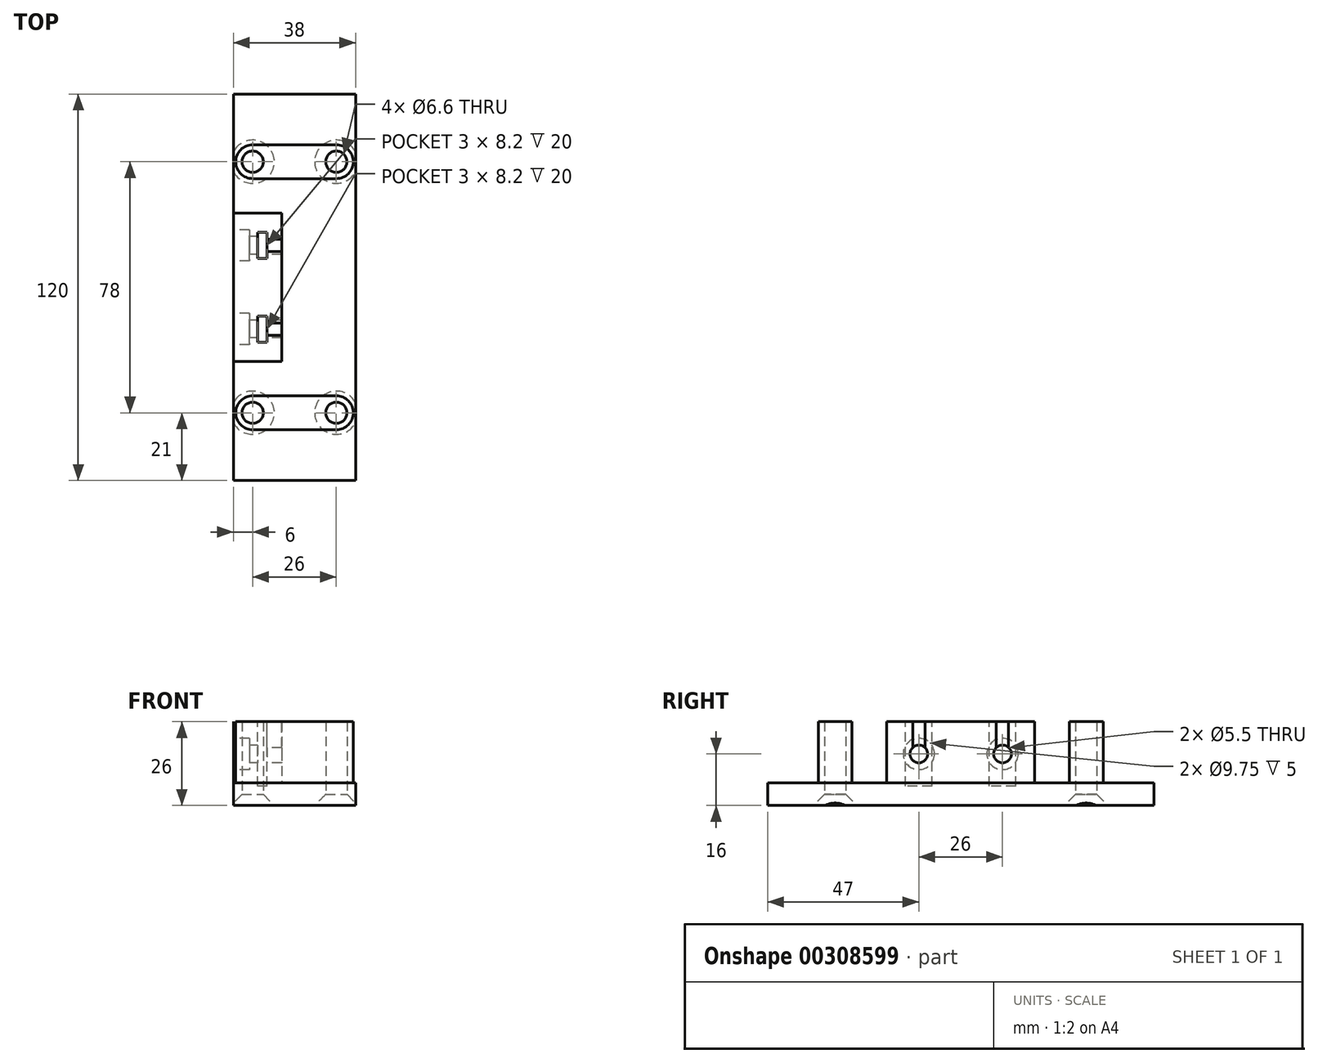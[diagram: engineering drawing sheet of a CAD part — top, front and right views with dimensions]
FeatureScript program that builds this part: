
annotation { "Feature Type Name" : "Feature", "Feature Type Description" : "" }
export const myFeature = defineFeature(function(context is Context, id is Id, definition is map)
    precondition{}
    {
        {
            var Q0;
            Q0=qCreatedBy(makeId("Top.planeOp"),FACE);
            var sketch = newSketch(context, id + "F0", { "sketchPlane" : qUnion([Q0])});
            skCircle(sketch, "E0", {"center": v(0, 0) * mm, "radius": 70.5 * mm});
            skCircle(sketch, "E1", {"center": v(0, 0) * mm, "radius": 60.75 * mm});
            skLineSegment(sketch, "E2", {"start": v(0, 0) * mm, "end": v(-222, 0) * mm, "construction": true});
            skPoint(sketch, "E3", {"position": v(-80, 0) * mm});
            skCircle(sketch, "E4", {"center": v(0, 0) * mm, "radius": 63.9 * mm});
            skPoint(sketch, "E5", {"position": v(-66.29, 24) * mm});
            skPoint(sketch, "E6", {"position": v(-55.8, 24) * mm});
            skPoint(sketch, "E7", {"position": v(-99, 0) * mm});
            skLineSegment(sketch, "E8.bottom", {"start": v(-118, 45.5) * mm, "end": v(-80, 45.5) * mm, "construction": true});
            skLineSegment(sketch, "E8.top", {"start": v(-118, -45.5) * mm, "end": v(-80, -45.5) * mm, "construction": true});
            skLineSegment(sketch, "E8.left", {"start": v(-118, 45.5) * mm, "end": v(-118, -45.5) * mm, "construction": true});
            skLineSegment(sketch, "E8.right", {"start": v(-80, 45.5) * mm, "end": v(-80, -45.5) * mm, "construction": true});
            skLineSegment(sketch, "E9.bottom", {"start": v(-86, 39) * mm, "end": v(-112, 39) * mm, "construction": true});
            skLineSegment(sketch, "E9.top", {"start": v(-86, -39) * mm, "end": v(-112, -39) * mm});
            skLineSegment(sketch, "E9.left", {"start": v(-86, 44) * mm, "end": v(-86, -44) * mm, "construction": true});
            skLineSegment(sketch, "E9.right", {"start": v(-112, 44) * mm, "end": v(-112, -44) * mm, "construction": true});
            skCircle(sketch, "E10", {"center": v(-112, 39) * mm, "radius": 2.5 * mm});
            skCircle(sketch, "E11", {"center": v(-86, 39) * mm, "radius": 2.5 * mm});
            skCircle(sketch, "E12", {"center": v(-112, -39) * mm, "radius": 2.5 * mm});
            skCircle(sketch, "E13", {"center": v(-86, -39) * mm, "radius": 2.5 * mm});
            skLineSegment(sketch, "E14.bottom", {"start": v(-80, 60) * mm, "end": v(-118, 60) * mm});
            skLineSegment(sketch, "E14.top", {"start": v(-80, -60) * mm, "end": v(-118, -60) * mm});
            skLineSegment(sketch, "E14.left", {"start": v(-80, 60) * mm, "end": v(-80, -60) * mm});
            skLineSegment(sketch, "E14.right", {"start": v(-118, 60) * mm, "end": v(-118, -60) * mm});
            skLineSegment(sketch, "E15", {"start": v(-118, 23) * mm, "end": v(-103, 23) * mm});
            skLineSegment(sketch, "E16", {"start": v(-103, 23) * mm, "end": v(-103, -23) * mm});
            skLineSegment(sketch, "E17", {"start": v(-103, -23) * mm, "end": v(-118, -23) * mm});
            skLineSegment(sketch, "E18.0", {"start": v(-112, 33.75) * mm, "end": v(-86, 33.75) * mm});
            skLineSegment(sketch, "E19.0", {"start": v(-112, 44.25) * mm, "end": v(-86, 44.25) * mm});
            skArc(sketch, "E20.0", {"start": v(-86, 33.75) * mm, "mid": v(-80.75, 39) * mm, "end": v(-86, 44.25) * mm});
            skArc(sketch, "E21.0", {"start": v(-112, 44.25) * mm, "mid": v(-117.25, 39) * mm, "end": v(-112, 33.75) * mm});
            skLineSegment(sketch, "E22.0", {"start": v(-112, -44.25) * mm, "end": v(-86, -44.25) * mm});
            skLineSegment(sketch, "E23.0", {"start": v(-112, -33.75) * mm, "end": v(-86, -33.75) * mm});
            skArc(sketch, "E24.0", {"start": v(-86, -44.25) * mm, "mid": v(-80.75, -39) * mm, "end": v(-86, -33.75) * mm});
            skArc(sketch, "E25.0", {"start": v(-112, -33.75) * mm, "mid": v(-117.25, -39) * mm, "end": v(-112, -44.25) * mm});
            skSolve(sketch);
        }
        {
            var Q0;
            Q0=makeQuery(id+"F0.imprint","IMPRINT",FACE,{"disambiguationData":[TD([[makeQuery(id+"F0.imprint","IMPRINT",EDGE,{"derivedFrom":sQuery(id+"F0.wireOp",EDGE,"E14.bottom")}),1.0]])]});
            var Q1;
            Q1=makeQuery(id+"F0.imprint","IMPRINT",FACE,{"disambiguationData":[TD([[makeQuery(id+"F0.imprint","IMPRINT",EDGE,{"derivedFrom":sQuery(id+"F0.wireOp",EDGE,"E10")}),-1.0]])]});
            var Q2;
            Q2=makeQuery(id+"F0.imprint","IMPRINT",FACE,{"disambiguationData":[TD([[makeQuery(id+"F0.imprint","IMPRINT",EDGE,{"derivedFrom":sQuery(id+"F0.wireOp",EDGE,"E12")}),-1.0]])]});
            var Q3;
            {var subQ0=sQuery(id+"F0.wireOp",EDGE,"E14.left");Q3=makeQuery(id+"F0.imprint","IMPRINT",FACE,{"disambiguationData":[TD([[makeQuery(id+"F0.imprint","IMPRINT",EDGE,{"derivedFrom":subQ0}),-1.0]])]});}
            var Q4;
            {var subQ4=sQuery(id+"F0.wireOp",EDGE,"KBghVLGI-IBoR-Y7Qn-Sn5X-7CIq2MfFH8mp");Q4=makeQuery(id+"F0.imprint","IMPRINT",FACE,{"disambiguationData":[TD([[makeQuery(id+"F0.imprint","IMPRINT",EDGE,{"derivedFrom":subQ4}),-1.0]])]});}
            var Q5;
            {var subQ0=sQuery(id+"F0.wireOp",EDGE,"E15");Q5=makeQuery(id+"F0.imprint","IMPRINT",FACE,{"disambiguationData":[TD([[makeQuery(id+"F0.imprint","IMPRINT",EDGE,{"derivedFrom":subQ0}),-1.0]])]});}
            var Q6;
            Q6=makeQuery(id+"F0.imprint","IMPRINT",FACE,{"disambiguationData":[TD([[makeQuery(id+"F0.imprint","IMPRINT",EDGE,{"derivedFrom":sQuery(id+"F0.wireOp",EDGE,"E10")}),1.0]])]});
            var Q7;
            Q7=makeQuery(id+"F0.imprint","IMPRINT",FACE,{"disambiguationData":[TD([[makeQuery(id+"F0.imprint","IMPRINT",EDGE,{"derivedFrom":sQuery(id+"F0.wireOp",EDGE,"E11")}),1.0]])]});
            var Q8;
            Q8=makeQuery(id+"F0.imprint","IMPRINT",FACE,{"disambiguationData":[TD([[makeQuery(id+"F0.imprint","IMPRINT",EDGE,{"derivedFrom":sQuery(id+"F0.wireOp",EDGE,"E12")}),1.0]])]});
            var Q9;
            Q9=makeQuery(id+"F0.imprint","IMPRINT",FACE,{"disambiguationData":[TD([[makeQuery(id+"F0.imprint","IMPRINT",EDGE,{"derivedFrom":sQuery(id+"F0.wireOp",EDGE,"E13")}),1.0]])]});
            extrude(context, id + "F1", {"entities" : qUnion([Q0, Q1, Q2, Q3, Q4, Q5, Q6, Q7, Q8, Q9]), "oppositeDirection" : true, "depth" : 7 * mm});
        }
        {
            var Q0;
            Q0=makeQuery(id+"F0.imprint","IMPRINT",FACE,{"disambiguationData":[TD([[makeQuery(id+"F0.imprint","IMPRINT",EDGE,{"derivedFrom":sQuery(id+"F0.wireOp",EDGE,"E10")}),-1.0]])]});
            var Q1;
            Q1=makeQuery(id+"F0.imprint","IMPRINT",FACE,{"disambiguationData":[TD([[makeQuery(id+"F0.imprint","IMPRINT",EDGE,{"derivedFrom":sQuery(id+"F0.wireOp",EDGE,"E12")}),-1.0]])]});
            var Q2;
            {var subQ4=sQuery(id+"F0.wireOp",EDGE,"M0PFJ9md-hpQt-fyBM-LhAF-8okodVHzGZRp");Q2=makeQuery(id+"F0.imprint","IMPRINT",FACE,{"disambiguationData":[TD([[makeQuery(id+"F0.imprint","IMPRINT",EDGE,{"derivedFrom":subQ4}),1.0]])]});}
            var Q3;
            {var subQ4=sQuery(id+"F0.wireOp",EDGE,"KBghVLGI-IBoR-Y7Qn-Sn5X-7CIq2MfFH8mp");Q3=makeQuery(id+"F0.imprint","IMPRINT",FACE,{"disambiguationData":[TD([[makeQuery(id+"F0.imprint","IMPRINT",EDGE,{"derivedFrom":subQ4}),-1.0]])]});}
            var Q4;
            {var subQ0=sQuery(id+"F0.wireOp",EDGE,"E15");Q4=makeQuery(id+"F0.imprint","IMPRINT",FACE,{"disambiguationData":[TD([[makeQuery(id+"F0.imprint","IMPRINT",EDGE,{"derivedFrom":subQ0}),-1.0]])]});}
            var Q5;
            Q5=makeQuery(id+"F0.imprint","IMPRINT",FACE,{"disambiguationData":[TD([[makeQuery(id+"F0.imprint","IMPRINT",EDGE,{"derivedFrom":sQuery(id+"F0.wireOp",EDGE,"E10")}),1.0]])]});
            var Q6;
            Q6=makeQuery(id+"F0.imprint","IMPRINT",FACE,{"disambiguationData":[TD([[makeQuery(id+"F0.imprint","IMPRINT",EDGE,{"derivedFrom":sQuery(id+"F0.wireOp",EDGE,"E11")}),1.0]])]});
            var Q7;
            Q7=makeQuery(id+"F0.imprint","IMPRINT",FACE,{"disambiguationData":[TD([[makeQuery(id+"F0.imprint","IMPRINT",EDGE,{"derivedFrom":sQuery(id+"F0.wireOp",EDGE,"E13")}),1.0]])]});
            var Q8;
            Q8=makeQuery(id+"F0.imprint","IMPRINT",FACE,{"disambiguationData":[TD([[makeQuery(id+"F0.imprint","IMPRINT",EDGE,{"derivedFrom":sQuery(id+"F0.wireOp",EDGE,"E12")}),1.0]])]});
            extrude(context, id + "F2", {"entities" : qUnion([Q0, Q1, Q2, Q3, Q4, Q5, Q6, Q7, Q8]), "operationType" : NewBodyOperationType.ADD, "depth" : 19 * mm, "offsetDistance" : 25 * mm});
        }
        {
            var Q0;
            {var subQ0=sQuery(id+"F0.wireOp",EDGE,"E14.right");Q0=makeQuery(id+"F2.boolean.opBoolean","MERGE",FACE,{"derivedFrom":[makeQuery(id+"F1.opExtrude","SWEPT_FACE",FACE,{"disambiguationData":[OSD([subQ0])]}),makeQuery(id+"F2.opExtrude","SWEPT_FACE",FACE,{"disambiguationData":[OSD([subQ0])]})]});}
            var sketch = newSketch(context, id + "F3", { "sketchPlane" : qUnion([Q0])});
            skPoint(sketch, "E26", {"position": v(-13, 9) * mm});
            skPoint(sketch, "E27", {"position": v(13, 9) * mm});
            skSolve(sketch);
        }
        {
            var Q0;
            Q0=sQuery(id+"F3.wireOp",VERTEX,"E26");
            var Q1;
            Q1=sQuery(id+"F3.wireOp",VERTEX,"E27");
            var Q2;
            Q2=makeQuery(id+"F1.opExtrude","SWEPT_BODY",BODY,{"disambiguationData":[OSD([sQuery(id+"F0.wireOp",EDGE,"E10"),sQuery(id+"F0.wireOp",EDGE,"E11"),sQuery(id+"F0.wireOp",EDGE,"E12"),sQuery(id+"F0.wireOp",EDGE,"E13"),sQuery(id+"F0.wireOp",EDGE,"E14.bottom"),sQuery(id+"F0.wireOp",EDGE,"E14.top"),sQuery(id+"F0.wireOp",EDGE,"E14.left"),sQuery(id+"F0.wireOp",EDGE,"E14.right")])]});
            hole(context, id + "F4", {"style" : HoleStyle.C_BORE, "endStyle" : HoleEndStyle.THROUGH, "standardTappedOrClearance" : lookupTablePath({ "standard" : "ISO", "fit" : "Normal", "size" : "M5", "type" : "Clearance" }), "standardBlindInLast" : lookupTablePath({ "fit" : "Standard", "standard" : "ISO", "size" : "M5", "type" : "Clearance" }), "holeDiameter" : 5.5 * mm, "cBoreDiameter" : 9.75 * mm, "cBoreDepth" : 5 * mm, "isTappedThrough" : true, "tappedDepth" : 12 * mm, "tapClearance" : 3, "locations" : qUnion([Q0, Q1]), "scope" : qUnion([Q2])});
        }
        {
            var Q0;
            Q0=makeQuery(id+"F2.opExtrude","CAP_FACE",FACE,{"disambiguationData":[OSD([sQuery(id+"F0.wireOp",EDGE,"E14.right"),sQuery(id+"F0.wireOp",EDGE,"E15"),sQuery(id+"F0.wireOp",EDGE,"E16"),sQuery(id+"F0.wireOp",EDGE,"E17")])],"isStart":false});
            var sketch = newSketch(context, id + "F5", { "sketchPlane" : qUnion([Q0])});
            skLineSegment(sketch, "E28", {"start": v(-118, 13) * mm, "end": v(-103, 13) * mm, "construction": true});
            skLineSegment(sketch, "E29", {"start": v(-118, -13) * mm, "end": v(-103, -13) * mm, "construction": true});
            skLineSegment(sketch, "E30", {"start": v(-109, 13) * mm, "end": v(-109, -13) * mm, "construction": true});
            skLineSegment(sketch, "E31.bottom", {"start": v(-107.5, 17.1) * mm, "end": v(-110.5, 17.1) * mm});
            skLineSegment(sketch, "E31.top", {"start": v(-107.5, 8.9) * mm, "end": v(-110.5, 8.9) * mm});
            skLineSegment(sketch, "E31.left", {"start": v(-107.5, 17.1) * mm, "end": v(-107.5, 8.9) * mm});
            skLineSegment(sketch, "E31.right", {"start": v(-110.5, 17.1) * mm, "end": v(-110.5, 8.9) * mm});
            skPoint(sketch, "E31.middle", {"position": v(-109, 13) * mm});
            skLineSegment(sketch, "E32.bottom", {"start": v(-107.5, -8.9) * mm, "end": v(-110.5, -8.9) * mm});
            skLineSegment(sketch, "E32.top", {"start": v(-107.5, -17.1) * mm, "end": v(-110.5, -17.1) * mm});
            skLineSegment(sketch, "E32.left", {"start": v(-107.5, -8.9) * mm, "end": v(-107.5, -17.1) * mm});
            skLineSegment(sketch, "E32.right", {"start": v(-110.5, -8.9) * mm, "end": v(-110.5, -17.1) * mm});
            skPoint(sketch, "E32.middle", {"position": v(-109, -13) * mm});
            skSolve(sketch);
        }
        {
            var Q0;
            Q0=makeQuery(id+"F5.imprint","IMPRINT",FACE,{"disambiguationData":[TD([[makeQuery(id+"F5.imprint","IMPRINT",EDGE,{"derivedFrom":sQuery(id+"F5.wireOp",EDGE,"E31.bottom")}),1.0]])]});
            var Q1;
            Q1=makeQuery(id+"F5.imprint","IMPRINT",FACE,{"disambiguationData":[TD([[makeQuery(id+"F5.imprint","IMPRINT",EDGE,{"derivedFrom":sQuery(id+"F5.wireOp",EDGE,"E32.bottom")}),1.0]])]});
            extrude(context, id + "F6", {"entities" : qUnion([Q0, Q1]), "operationType" : NewBodyOperationType.REMOVE, "oppositeDirection" : true, "depth" : 20 * mm});
        }
        {
            var Q0;
            Q0=makeQuery(id+"F1.opExtrude","CAP_FACE",FACE,{"disambiguationData":[OSD([sQuery(id+"F0.wireOp",EDGE,"E14.bottom"),sQuery(id+"F0.wireOp",EDGE,"E14.top"),sQuery(id+"F0.wireOp",EDGE,"E14.left"),sQuery(id+"F0.wireOp",EDGE,"E14.right")])],"isStart":false});
            var sketch = newSketch(context, id + "F7", { "sketchPlane" : qUnion([Q0])});
            skPoint(sketch, "E33.0", {"position": v(-86, -39) * mm});
            skPoint(sketch, "E34.0", {"position": v(-112, -39) * mm});
            skPoint(sketch, "E35.0", {"position": v(-112, 39) * mm});
            skPoint(sketch, "E36.0", {"position": v(-86, 39) * mm});
            skSolve(sketch);
        }
        {
            var Q0;
            Q0=sQuery(id+"F7.wireOp",VERTEX,"E33.0");
            var Q1;
            Q1=sQuery(id+"F7.wireOp",VERTEX,"E34.0");
            var Q2;
            Q2=sQuery(id+"F7.wireOp",VERTEX,"E35.0");
            var Q3;
            Q3=sQuery(id+"F7.wireOp",VERTEX,"E36.0");
            var Q4;
            Q4=makeQuery(id+"F1.opExtrude","SWEPT_BODY",BODY,{"disambiguationData":[OSD([sQuery(id+"F0.wireOp",EDGE,"E14.bottom"),sQuery(id+"F0.wireOp",EDGE,"E14.top"),sQuery(id+"F0.wireOp",EDGE,"E14.left"),sQuery(id+"F0.wireOp",EDGE,"E14.right")])]});
            hole(context, id + "F8", {"style" : HoleStyle.C_SINK, "endStyle" : HoleEndStyle.BLIND, "standardTappedOrClearance" : lookupTablePath({ "standard" : "ISO", "fit" : "Normal", "size" : "M6", "type" : "Clearance" }), "standardBlindInLast" : lookupTablePath({ "fit" : "Standard", "standard" : "ISO", "size" : "M6", "type" : "Clearance" }), "holeDiameter" : 6.6 * mm, "cSinkDiameter" : 13.44 * mm, "cSinkAngle" : 90 * degree, "holeDepth" : 40 * mm, "isTappedThrough" : true, "tappedDepth" : 12 * mm, "tapClearance" : 3, "locations" : qUnion([Q0, Q1, Q2, Q3]), "scope" : qUnion([Q4])});
        }
        {
            var Q0;
            Q0=makeQuery(id+"F2.opExtrude","CAP_FACE",FACE,{"disambiguationData":[OSD([sQuery(id+"F0.wireOp",EDGE,"E14.right"),sQuery(id+"F0.wireOp",EDGE,"E15"),sQuery(id+"F0.wireOp",EDGE,"E16"),sQuery(id+"F0.wireOp",EDGE,"E17")])],"isStart":false});
            var sketch = newSketch(context, id + "F9", { "sketchPlane" : qUnion([Q0])});
            skLineSegment(sketch, "E37.bottom", {"start": v(-103, 14.9) * mm, "end": v(-107.5, 14.9) * mm});
            skLineSegment(sketch, "E37.top", {"start": v(-103, 11.1) * mm, "end": v(-107.5, 11.1) * mm});
            skLineSegment(sketch, "E37.left", {"start": v(-103, 14.9) * mm, "end": v(-103, 11.1) * mm});
            skPoint(sketch, "E37.middle", {"position": v(-107.5, 13) * mm});
            skLineSegment(sketch, "E38.bottom", {"start": v(-103, -11.1) * mm, "end": v(-107.5, -11.1) * mm});
            skLineSegment(sketch, "E38.top", {"start": v(-103, -14.9) * mm, "end": v(-107.5, -14.9) * mm});
            skLineSegment(sketch, "E38.left", {"start": v(-103, -11.1) * mm, "end": v(-103, -14.9) * mm});
            skPoint(sketch, "E38.middle", {"position": v(-107.5, -13) * mm});
            skLineSegment(sketch, "E39", {"start": v(-107.5, 14.9) * mm, "end": v(-107.5, 11.1) * mm});
            skLineSegment(sketch, "E40", {"start": v(-107.5, -11.1) * mm, "end": v(-107.5, -14.9) * mm});
            skSolve(sketch);
        }
        {
            var Q0;
            Q0=makeQuery(id+"F9.imprint","IMPRINT",FACE,{"disambiguationData":[TD([[makeQuery(id+"F9.imprint","IMPRINT",EDGE,{"derivedFrom":sQuery(id+"F9.wireOp",EDGE,"E37.bottom")}),1.0]])]});
            var Q1;
            Q1=makeQuery(id+"F9.imprint","IMPRINT",FACE,{"disambiguationData":[TD([[makeQuery(id+"F9.imprint","IMPRINT",EDGE,{"derivedFrom":sQuery(id+"F9.wireOp",EDGE,"E38.bottom")}),1.0]])]});
            extrude(context, id + "F10", {"entities" : qUnion([Q0, Q1]), "operationType" : NewBodyOperationType.REMOVE, "oppositeDirection" : true, "depth" : 10 * mm, "offsetDistance" : 25 * mm});
        }
    });
